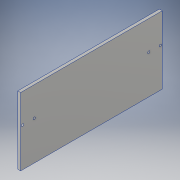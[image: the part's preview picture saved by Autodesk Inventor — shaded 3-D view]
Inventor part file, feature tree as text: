
AUTODESK INVENTOR PART (.ipt)
format: ipt  version: 2017 (Build 210142000, 142)  size: 107,520 bytes
history: native  units: in
note: dims shown in document units (in); Inventor stores cm internally (conversion verified against a paired STEP export)
features: sketch x2, extrude x1, hole x1, plane x1, projected_geometry x1
ambient origin geometry x8: Origin, YZ Plane, XZ Plane, XY Plane, X Axis, Y Axis, Z Axis, Center Point
bodies: Solid1 (feature_tree)
feature tree (6):
  extrude  "Extrusion1"  Depth=9.125in
  hole  "Hole1"  [1 undecoded]
  plane  "Work Plane1"
  sketch  "Sketch1"  dims[d0=4.375in d1=9.125in]
  sketch  "Sketch2"  dims[d2=0.1875in d3=0.0in d4=2.5in d5=2.5in d6=2.5in d7=2.5in d8=0.125in d9=0.75in d10=0.75in d11=0.125in d12=0.145in d13=0.75in d14=0.75in d15=0.188in d16=0.5635in d17=1.0in d18=0.8108in]
  projected_geometry  "Projected Loop1"
note: 1 required parameter value undecoded (feature->parameter linkage not recoverable at this tier; creation-order binding heuristic only, values carry confidence <= 0.55)
